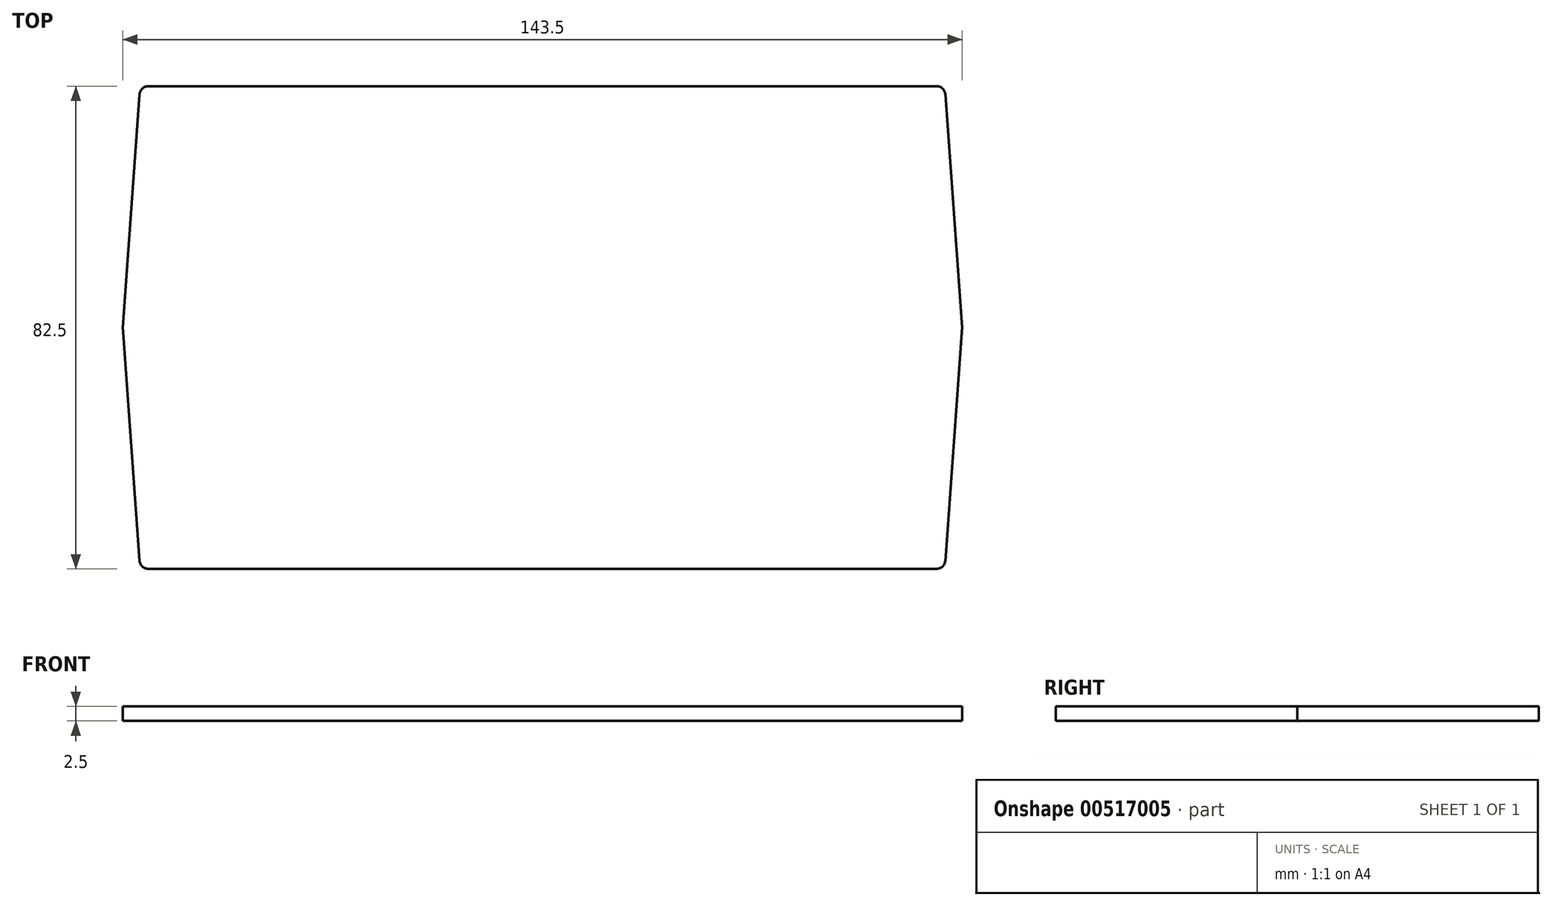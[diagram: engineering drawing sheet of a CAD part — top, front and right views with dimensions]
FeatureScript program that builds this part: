
annotation { "Feature Type Name" : "Feature", "Feature Type Description" : "" }
export const myFeature = defineFeature(function(context is Context, id is Id, definition is map)
    precondition{}
    {
        {
            var Q0;
            Q0=qCreatedBy(makeId("Top.planeOp"),FACE);
            var sketch = newSketch(context, id + "F0", { "sketchPlane" : qUnion([Q0])});
            skLineSegment(sketch, "E0", {"start": v(-71.75, 0) * mm, "end": v(71.75, 0) * mm, "construction": true});
            skLineSegment(sketch, "E1", {"start": v(0, 41.25) * mm, "end": v(0, -41.25) * mm, "construction": true});
            skLineSegment(sketch, "E2.bottom", {"start": v(68.75, 41.25) * mm, "end": v(-68.75, 41.25) * mm});
            skLineSegment(sketch, "E2.top", {"start": v(68.75, -41.25) * mm, "end": v(-68.75, -41.25) * mm});
            skLineSegment(sketch, "E2.left", {"start": v(71.75, 41.25) * mm, "end": v(71.75, -41.25) * mm, "construction": true});
            skLineSegment(sketch, "E2.right", {"start": v(-71.75, 41.25) * mm, "end": v(-71.75, -41.25) * mm, "construction": true});
            skPoint(sketch, "E2.middle", {"position": v(0, 0) * mm});
            skLineSegment(sketch, "E3", {"start": v(71.75, 0) * mm, "end": v(68.75, 41.25) * mm});
            skLineSegment(sketch, "E4", {"start": v(71.75, 0) * mm, "end": v(68.75, -41.25) * mm});
            skLineSegment(sketch, "E5", {"start": v(-71.75, 0) * mm, "end": v(-68.75, 41.25) * mm});
            skLineSegment(sketch, "E6", {"start": v(-71.75, 0) * mm, "end": v(-68.75, -41.25) * mm});
            skSolve(sketch);
        }
        {
            var Q0;
            Q0 = qSketchRegion(id + "F0", true);
            extrude(context, id + "F1", {"entities" : qUnion([Q0]), "depth" : 2.5 * mm, "offsetDistance" : 25 * mm});
        }
        {
            var Q0;
            Q0=makeQuery(id+"F1.opExtrude","SWEPT_EDGE",EDGE,{"disambiguationData":[OSD([sQuery(id+"F0.wireOp",EDGE,"E2.top"),sQuery(id+"F0.wireOp",EDGE,"E6")])]});
            var Q1;
            Q1=makeQuery(id+"F1.opExtrude","SWEPT_EDGE",EDGE,{"disambiguationData":[OSD([sQuery(id+"F0.wireOp",EDGE,"E2.bottom"),sQuery(id+"F0.wireOp",EDGE,"E5")])]});
            var Q2;
            Q2=makeQuery(id+"F1.opExtrude","SWEPT_EDGE",EDGE,{"disambiguationData":[OSD([sQuery(id+"F0.wireOp",EDGE,"E2.bottom"),sQuery(id+"F0.wireOp",EDGE,"E3")])]});
            var Q3;
            Q3=makeQuery(id+"F1.opExtrude","SWEPT_EDGE",EDGE,{"disambiguationData":[OSD([sQuery(id+"F0.wireOp",EDGE,"E2.top"),sQuery(id+"F0.wireOp",EDGE,"E4")])]});
            fillet(context, id + "F2", {"entities" : qUnion([Q0, Q1, Q2, Q3]), "radius" : 1.5 * mm, "tangentPropagation" : true, "allowEdgeOverflow" : false});
        }
    });
